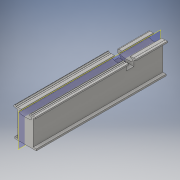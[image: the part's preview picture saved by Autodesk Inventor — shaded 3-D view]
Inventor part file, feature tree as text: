
AUTODESK INVENTOR PART (.ipt)
format: ipt  version: 2016 (Build 200138000, 138)  size: 335,872 bytes
history: native  units: in
note: dims shown in document units (in); Inventor stores cm internally (conversion verified against a paired STEP export)
features: extrude x6, sketch x6, chamfer x1, plane x1
ambient origin geometry x8: Origin, YZ Plane, XZ Plane, XY Plane, X Axis, Y Axis, Z Axis, Center Point
bodies: Solid1 (feature_tree)
feature tree (14):
  extrude  "Extrusion1"  TaperAngle=150.0deg  [1 undecoded]
  chamfer  "Chamfer1"  Distance=0.4016in
  plane  "Work Plane3"
  extrude  "Extrusion2"  Depth=0.962in
  extrude  "Extrusion3"  Depth=0.126in
  extrude  "Extrusion4"  Depth=0.6339in
  extrude  "Extrusion5"  Depth=0.0787in
  extrude  "Extrusion6"  Depth=0.9921in
  sketch  "Sketch1"  dims[d0=0.4331in d1=150.0deg]
  sketch  "Sketch2"  dims[d2=0.3937in]
  sketch  "Sketch3"  dims[d3=0.4606in]
  sketch  "Sketch4"  dims[d4=0.4961in]
  sketch  "Sketch5"  dims[d5=0.962in]
  sketch  "Sketch6"  dims[d6=0.1496in d7=0.4016in d8=0.962in d9=0.126in d10=0.6339in d11=0.0787in d12=0.9921in d13=0.6181in d14=0.5787in d15=0.315in d16=120.0deg d17=0.1575in d18=2.4409in d19=8.0315in d22=3.6299in d24=0.5in d25=1.4252in d26=180.0deg d27=0.0787in d28=0.748in d29=0.0787in d30=0.5197in d31=0.962in d32=0.1811in d33=0.6299in d34=0.9615in d35=0.5512in d36=0.5512in d37=90.0deg d38=0.1181in d39=60.0deg d40=0.7244in d41=0.8858in d42=0.374in d43=5.748in d44=90.0deg d45=0.374in d46=2.185in d47=90.0deg d48=0.374in d49=1.6929in d50=90.0deg d51=1.378in d52=180.0deg d53=0.7087in d54=90.0deg d55=1.378in d57=0.7087in d58=0.4173in d59=180.0deg d60=0.315in d61=120.0deg d62=2.4409in d63=55.9055in d64=0.0in d65=0.3543in d66=0.0787in d67=45.0deg d68=40.1575in d69=3.2283in d70=3.4528in d71=55.9055in d72=0.0in d73=55.9055in d74=0.0in d75=55.9055in d76=0.0in d77=2.7953in d78=1.2205in d79=1.7323in d80=55.9055in d81=0.0in d82=1.0236in d83=0.0in]
note: 1 required parameter value undecoded (feature->parameter linkage not recoverable at this tier; creation-order binding heuristic only, values carry confidence <= 0.55)
